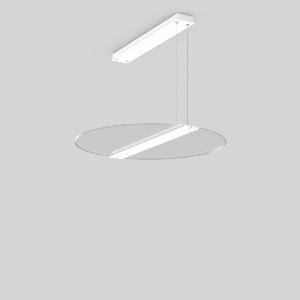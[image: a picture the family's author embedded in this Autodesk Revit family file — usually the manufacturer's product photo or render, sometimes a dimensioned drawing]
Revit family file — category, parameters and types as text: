
# Revit family: twindot_s_round_312353_002_1_730_b87a
name_source: partatom
category: Lighting Fixtures
units: mm (PartAtom-declared; Revit-internal decimal feet)

## family parameters
Cut with Voids When Loaded = No
Host = Face
Light Source = No
Part Type = Normal
Room Calculation Point = No
Round Connector Dimension = Use Diameter
Shared = No

## types (1)
- TWINDOT S round (1 x LED Modul 840, 4500 lm, 4000)
    Apparent Load = 39 VA
    CIE Flux Codes = 49 78 94 56 100
    Color Rendering = 80
    Color Temperature = 4000
    Default Elevation = 1800 mm
    Description = Series: TWINDOT S round
LED pendant luminaire with extremely flat and frameless appearance. Middle bar made of aluminium extrusion profile, powder-coated. Transparent light guide made of UV-resistant acrylic glass (PMMA) with TWINDOT prismatic. Light control with perfectly glare-free TWINDOT technology for pleasantly gentle light with soft shadows. Even and wide indirect and direct light distribution. Direct 55%, indirect 45% light emission. 4-point steel cable suspension, steplessly adjustable. Converter integrated in the canopy (powder-coated white). Power supply through suspension cable. 
Colour: traffic white, matt (RAL 9016)
Diameter: 645 mm
Height: 20 mm
Suspension length: 500-1200 mm
Lamp: LED
Socket: without socket
Colour temperature: 4000K
Colour rendering index (CRI): 80
System power: 39 W
Rated luminous flux: 4500 lm
Luminous efficiency: 115 lm/W
Control gear: Dimmable Bluetooth converter
Protection class: I
Type of protection: IP 20
    Height = 20 mm  [stored 0.0656168 ft]
    Lamp = 1 x LED Modul 840
    Lamp Light Flux = 4500 lm
    Lamp count = 1
    Length = 645 mm
    Lifetime = 50000 h
    Luminous efficacy = 115 lm/W
    Manufacturer = RZB
    ModVariant = No
    Model = 312353.002.1.730
    Mounting Place = Ceiling
    Mounting Type = Pendant
    Number of Poles = 1
    OnlyDefault = Yes
    Power Factor = 1
    Product Name = TWINDOT S round
    Product group = Pendant modular luminaires
    ProductGroupID = 906
    Protection Class = Protection class I
    Protection Degree = IP 20
    RLX_Detail_Level = 1
    RLX_Emergency_Light_Flux = 0 lm
    RLX_Emergency_Type = 0
    RLX_Emergency_Type_DB = No
    RlxData = <blob elided: 36253 chars, md5=ca013abb>
    Socket = socket
    Standby Power = 0 W
    System Light Flux = 4500 lm
    System Power = 39 W
    Type Comments = Product without accessories
    Type Image = 312353.002.jpg
    URL = http://relux.com
    VarID = ---
    Voltage = 230 V
    Voltage Range = 220-240 V
    Weight = 0.00 kg
    Width = 0 mm  [stored 0 ft]

note: [stored X ft] marks values corroborated as IEEE doubles in the binary element streams (Revit-internal decimal feet)

## geometry (parser evidence)
native form markers: Blend x4, Sweep x13
no freeform markers — native parametric forms only
